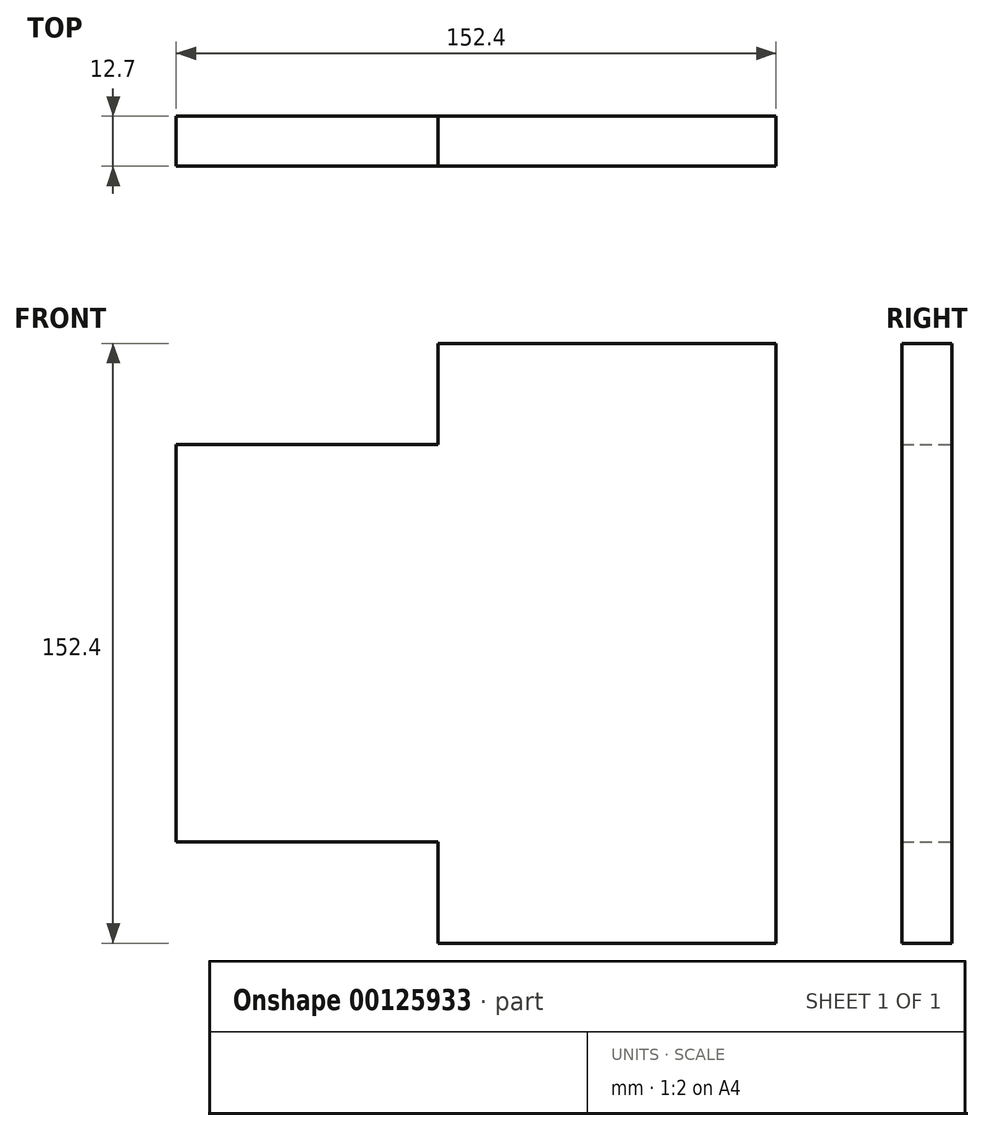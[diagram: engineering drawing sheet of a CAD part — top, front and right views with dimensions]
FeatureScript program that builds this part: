
annotation { "Feature Type Name" : "Feature", "Feature Type Description" : "" }
export const myFeature = defineFeature(function(context is Context, id is Id, definition is map)
    precondition{}
    {
        {
            var Q0;
            Q0=qCreatedBy(makeId("Front.planeOp"),FACE);
            var sketch = newSketch(context, id + "F0", { "sketchPlane" : qUnion([Q0])});
            skLineSegment(sketch, "E0.right", {"start": v(75.91, 0) * mm, "end": v(75.91, 152.4) * mm});
            skLineSegment(sketch, "E1", {"start": v(-76.49, 126.72) * mm, "end": v(-10.03, 126.72) * mm});
            skLineSegment(sketch, "E2", {"start": v(-10.03, 126.72) * mm, "end": v(-10.03, 152.4) * mm});
            skLineSegment(sketch, "E3", {"start": v(-10.03, 152.4) * mm, "end": v(75.91, 152.4) * mm});
            skLineSegment(sketch, "E4", {"start": v(-10.03, 0) * mm, "end": v(-10.03, 25.78) * mm});
            skLineSegment(sketch, "E5", {"start": v(-10.03, 25.78) * mm, "end": v(-76.49, 25.78) * mm});
            skLineSegment(sketch, "E6", {"start": v(-76.49, 25.78) * mm, "end": v(-76.49, 126.72) * mm});
            skLineSegment(sketch, "E7", {"start": v(-10.03, 0) * mm, "end": v(75.91, 0) * mm});
            skSolve(sketch);
        }
        {
            var Q0;
            Q0=qSketchRegion(id+"F0",true);
            extrude(context, id + "F1", {"entities" : qUnion([Q0]), "depth" : 12.7 * mm});
        }
    });
